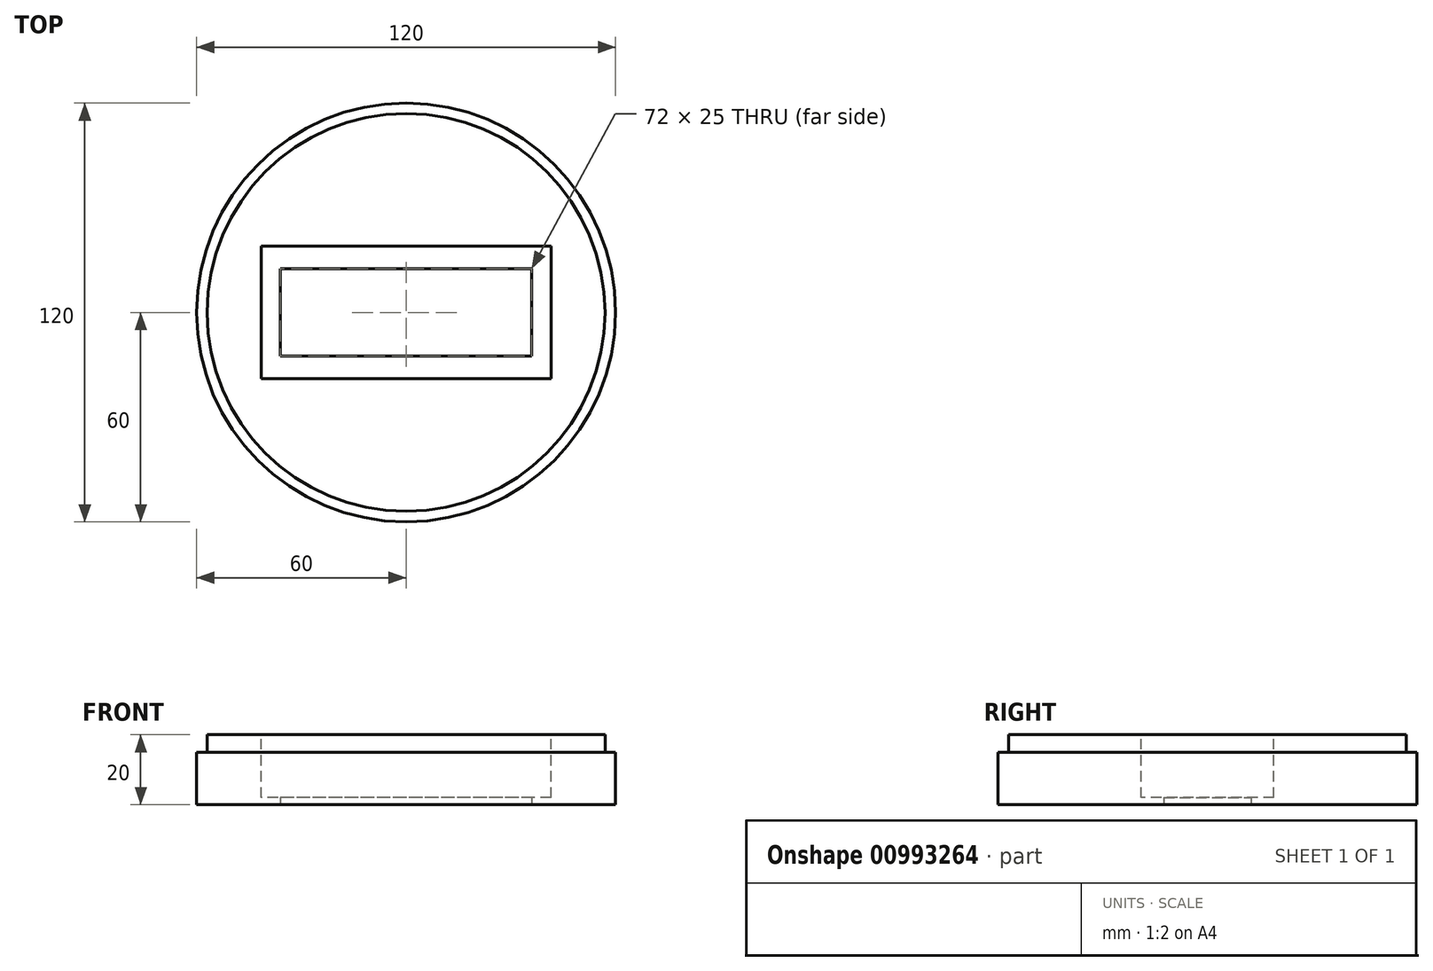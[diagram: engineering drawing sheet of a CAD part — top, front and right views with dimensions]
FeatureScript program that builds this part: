
annotation { "Feature Type Name" : "Feature", "Feature Type Description" : "" }
export const myFeature = defineFeature(function(context is Context, id is Id, definition is map)
    precondition{}
    {
        {
            var Q0;
            Q0=qCreatedBy(makeId("Top.planeOp"),FACE);
            var sketch = newSketch(context, id + "F0", { "sketchPlane" : qUnion([Q0])});
            skCircle(sketch, "E0", {"center": v(0, 0) * mm, "radius": 60 * mm});
            skCircle(sketch, "E1", {"center": v(0, 0) * mm, "radius": 57 * mm});
            skSolve(sketch);
        }
        {
            var Q0;
            Q0=qCreatedBy(makeId("Top.planeOp"),FACE);
            var sketch = newSketch(context, id + "F1", { "sketchPlane" : qUnion([Q0])});
            skCircle(sketch, "E2", {"center": v(0, 0) * mm, "radius": 54 * mm});
            skCircle(sketch, "E3", {"center": v(0, 0) * mm, "radius": 57 * mm});
            skSolve(sketch);
        }
        {
            var Q0;
            Q0=makeQuery(id+"F0.imprint","IMPRINT",FACE,{"disambiguationData":[TD([[makeQuery(id+"F0.imprint","IMPRINT",EDGE,{"derivedFrom":sQuery(id+"F0.wireOp",EDGE,"E0")}),1.0]])]});
            extrude(context, id + "F2", {"entities" : qUnion([Q0]), "depth" : 15 * mm, "offsetDistance" : 25 * mm});
        }
        {
            var Q0;
            Q0=qSketchRegion(id+"F1",true);
            extrude(context, id + "F3", {"entities" : qUnion([Q0]), "operationType" : NewBodyOperationType.ADD, "depth" : 20 * mm, "offsetDistance" : 25 * mm});
        }
        {
            var Q0;
            Q0=qCreatedBy(makeId("Top.planeOp"),FACE);
            var sketch = newSketch(context, id + "F4", { "sketchPlane" : qUnion([Q0])});
            skCircle(sketch, "E4", {"center": v(0, 0) * mm, "radius": 57 * mm});
            skSolve(sketch);
        }
        {
            var Q0;
            Q0=qSketchRegion(id+"F4",true);
            var Q1;
            Q1=qSketchRegion(id+"F7",true);
            extrude(context, id + "F5", {"entities" : qUnion([Q0, Q1]), "operationType" : NewBodyOperationType.ADD, "depth" : 10 * mm, "offsetDistance" : 25 * mm});
        }
        {
            var Q0;
            Q0=qCreatedBy(makeId("Top.planeOp"),FACE);
            cPlane(context, id + "F6", {"entities" : qUnion([Q0]), "cplaneType" : CPlaneType.OFFSET, "offset" : 45 * mm, "width" : 150 * mm, "height" : 150 * mm});
        }
        {
            var Q0;
            Q0=qCreatedBy(id+"F6.planeOp",FACE);
            var sketch = newSketch(context, id + "F7", { "sketchPlane" : qUnion([Q0])});
            skCircle(sketch, "E5", {"center": v(0, 0) * mm, "radius": 54 * mm});
            skSolve(sketch);
        }
        {
            var Q0;
            Q0=qSketchRegion(id+"F7",true);
            extrude(context, id + "F8", {"entities" : qUnion([Q0]), "operationType" : NewBodyOperationType.REMOVE, "oppositeDirection" : true, "depth" : 40 * mm, "offsetDistance" : 25 * mm});
        }
        {
            var Q0;
            Q0=qCreatedBy(makeId("Right.planeOp"),FACE);
            var sketch = newSketch(context, id + "F9", { "sketchPlane" : qUnion([Q0])});
            skLineSegment(sketch, "E6", {"start": v(0, 0) * mm, "end": v(25, 0) * mm, "construction": true});
            skLineSegment(sketch, "E7", {"start": v(25, 0) * mm, "end": v(25, 65) * mm, "construction": true});
            skLineSegment(sketch, "E8.bottom", {"start": v(25, 65) * mm, "end": v(40, 65) * mm});
            skLineSegment(sketch, "E8.top", {"start": v(25, 55) * mm, "end": v(40, 55) * mm});
            skLineSegment(sketch, "E8.left", {"start": v(25, 65) * mm, "end": v(25, 55) * mm});
            skLineSegment(sketch, "E8.right", {"start": v(40, 65) * mm, "end": v(40, 55) * mm});
            skSolve(sketch);
        }
        {
            var Q0;
            Q0=makeQuery(id+"F9.imprint","IMPRINT",FACE,{"disambiguationData":[TD([[makeQuery(id+"F9.imprint","IMPRINT",EDGE,{"derivedFrom":sQuery(id+"F9.wireOp",EDGE,"E8.bottom")}),-1.0]])]});
            extrude(context, id + "F10", {"entities" : qUnion([Q0]), "operationType" : NewBodyOperationType.REMOVE, "depth" : 279.5 * mm, "offsetDistance" : 25 * mm});
        }
        {
            var Q0;
            Q0=makeQuery(id+"F1.imprint","IMPRINT",FACE,{"disambiguationData":[TD([[makeQuery(id+"F1.imprint","IMPRINT",EDGE,{"derivedFrom":sQuery(id+"F1.wireOp",EDGE,"E2")}),1.0]])]});
            extrude(context, id + "F11", {"entities" : qUnion([Q0]), "operationType" : NewBodyOperationType.REMOVE, "depth" : 71.5 * mm, "offsetDistance" : 25 * mm});
        }
        {
            var Q0;
            Q0=qCreatedBy(makeId("Top.planeOp"),FACE);
            cPlane(context, id + "F12", {"entities" : qUnion([Q0]), "cplaneType" : CPlaneType.OFFSET, "offset" : 15 * mm, "width" : 150 * mm, "height" : 150 * mm});
        }
        {
            var Q0;
            Q0=qCreatedBy(makeId("Top.planeOp"),FACE);
            var sketch = newSketch(context, id + "F13", { "sketchPlane" : qUnion([Q0])});
            skCircle(sketch, "E9", {"center": v(0, 0) * mm, "radius": 60 * mm});
            skSolve(sketch);
        }
        {
            var Q0;
            Q0=qSketchRegion(id+"F13",true);
            extrude(context, id + "F14", {"entities" : qUnion([Q0]), "operationType" : NewBodyOperationType.ADD, "depth" : 20 * mm, "offsetDistance" : 25 * mm});
        }
        {
            var Q0;
            Q0=qCreatedBy(makeId("Top.planeOp"),FACE);
            var sketch = newSketch(context, id + "F15", { "sketchPlane" : qUnion([Q0])});
            skLineSegment(sketch, "E10.bottom", {"start": v(36, -12.5) * mm, "end": v(-36, -12.5) * mm});
            skLineSegment(sketch, "E10.top", {"start": v(36, 12.5) * mm, "end": v(-36, 12.5) * mm});
            skLineSegment(sketch, "E10.left", {"start": v(36, -12.5) * mm, "end": v(36, 12.5) * mm});
            skLineSegment(sketch, "E10.right", {"start": v(-36, -12.5) * mm, "end": v(-36, 12.5) * mm});
            skPoint(sketch, "E10.middle", {"position": v(0, 0) * mm});
            skSolve(sketch);
        }
        {
            var Q0;
            Q0=makeQuery(id+"F15.imprint","IMPRINT",FACE,{"disambiguationData":[TD([[makeQuery(id+"F15.imprint","IMPRINT",EDGE,{"derivedFrom":sQuery(id+"F15.wireOp",EDGE,"E10.bottom")}),-1.0]])]});
            extrude(context, id + "F16", {"entities" : qUnion([Q0]), "operationType" : NewBodyOperationType.REMOVE, "depth" : 20 * mm, "offsetDistance" : 25 * mm});
        }
        {
            var Q0;
            Q0=qCreatedBy(id+"F12.planeOp",FACE);
            var sketch = newSketch(context, id + "F17", { "sketchPlane" : qUnion([Q0])});
            skLineSegment(sketch, "E11.bottom", {"start": v(41.5, 19) * mm, "end": v(-41.5, 19) * mm});
            skLineSegment(sketch, "E11.top", {"start": v(41.5, -19) * mm, "end": v(-41.5, -19) * mm});
            skLineSegment(sketch, "E11.left", {"start": v(41.5, 19) * mm, "end": v(41.5, -19) * mm});
            skLineSegment(sketch, "E11.right", {"start": v(-41.5, 19) * mm, "end": v(-41.5, -19) * mm});
            skPoint(sketch, "E11.middle", {"position": v(0, 0) * mm});
            skSolve(sketch);
        }
        {
            var Q0;
            Q0 = qSketchRegion(id + "F17", true);
            extrude(context, id + "F18", {"entities" : qUnion([Q0]), "operationType" : NewBodyOperationType.REMOVE, "oppositeDirection" : true, "depth" : 13 * mm, "offsetDistance" : 25 * mm, "hasSecondDirection" : true, "secondDirectionOppositeDirection" : false, "secondDirectionDepth" : 5 * mm});
        }
        {
            var Q0;
            Q0=makeQuery(id+"F14.boolean.opBoolean","MERGE",FACE,{"derivedFrom":[makeQuery(id+"F3.opExtrude","CAP_FACE",FACE,{"disambiguationData":[OSD([sQuery(id+"F1.wireOp",EDGE,"E2"),sQuery(id+"F1.wireOp",EDGE,"E3")])],"isStart":false}),makeQuery(id+"F14.opExtrude","CAP_FACE",FACE,{"disambiguationData":[OSD([sQuery(id+"F13.wireOp",EDGE,"E9")])],"isStart":false})]});
            var sketch = newSketch(context, id + "F19", { "sketchPlane" : qUnion([Q0])});
            skCircle(sketch, "E12", {"center": v(0, 0) * mm, "radius": 60 * mm});
            skCircle(sketch, "E13", {"center": v(0, 0) * mm, "radius": 57 * mm});
            skSolve(sketch);
        }
        {
            var Q0;
            Q0 = qSketchRegion(id + "F19", true);
            extrude(context, id + "F20", {"entities" : qUnion([Q0]), "operationType" : NewBodyOperationType.REMOVE, "oppositeDirection" : true, "depth" : 5 * mm, "offsetDistance" : 25 * mm});
        }
    });
